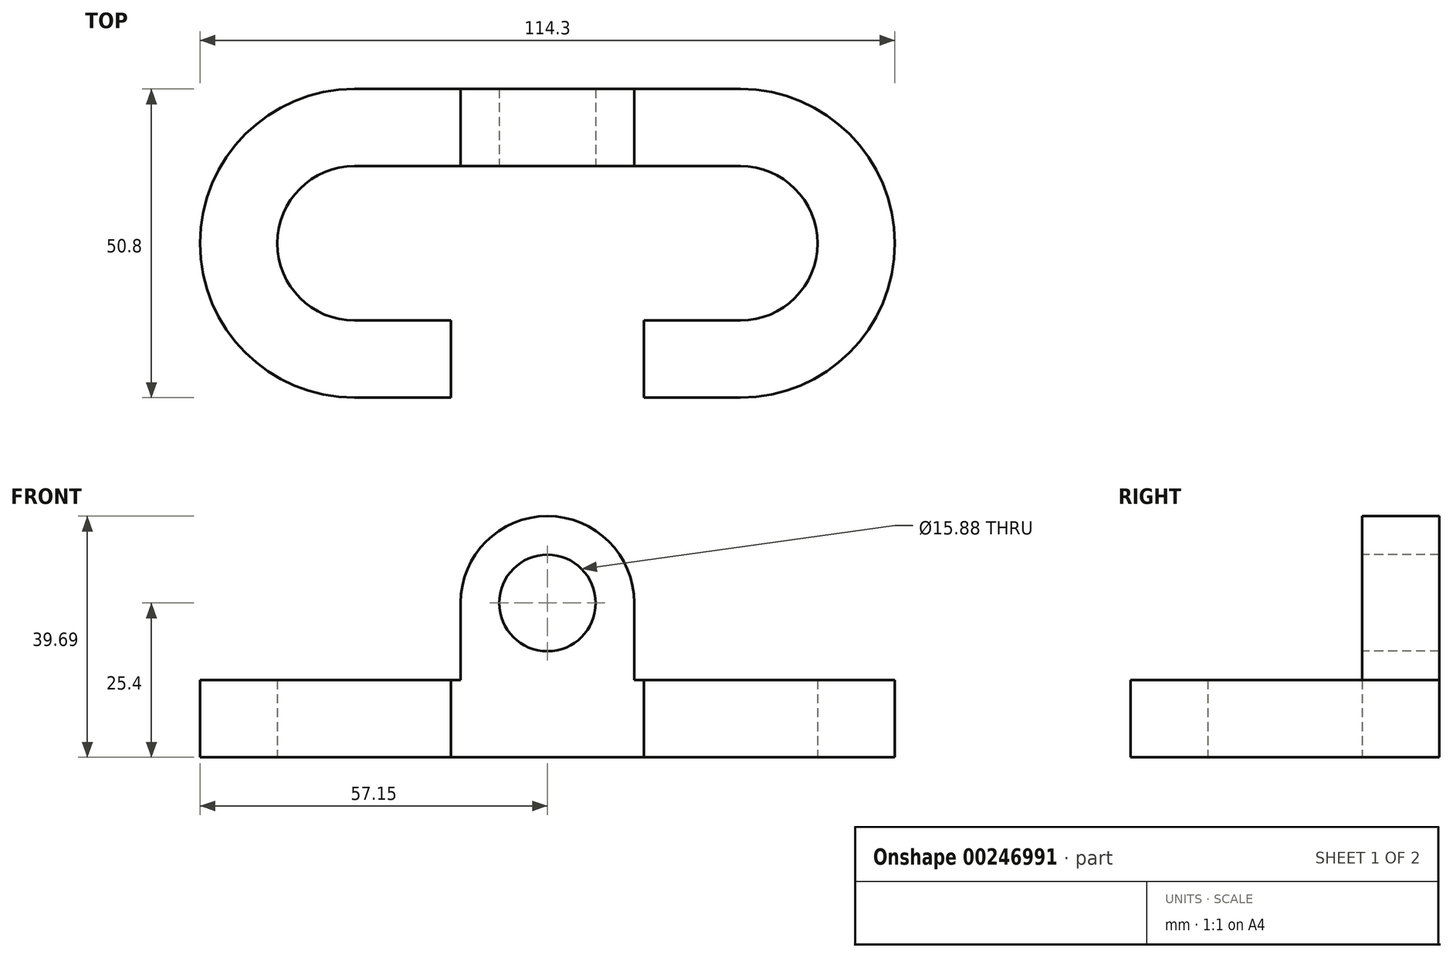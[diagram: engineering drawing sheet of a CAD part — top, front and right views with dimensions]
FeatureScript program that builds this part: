
annotation { "Feature Type Name" : "Feature", "Feature Type Description" : "" }
export const myFeature = defineFeature(function(context is Context, id is Id, definition is map)
    precondition{}
    {
        {
            var Q0;
            Q0=qCreatedBy(makeId("Top.planeOp"),FACE);
            var sketch = newSketch(context, id + "F0", { "sketchPlane" : qUnion([Q0])});
            skArc(sketch, "E0", {"start": v(31.75, -12.7) * mm, "mid": v(44.45, 0) * mm, "end": v(31.75, 12.7) * mm});
            skArc(sketch, "E1", {"start": v(31.75, -25.4) * mm, "mid": v(57.15, 0) * mm, "end": v(31.75, 25.4) * mm});
            skLineSegment(sketch, "E2", {"start": v(31.75, 25.4) * mm, "end": v(0, 25.4) * mm});
            skLineSegment(sketch, "E3", {"start": v(31.75, 12.7) * mm, "end": v(0, 12.7) * mm});
            skLineSegment(sketch, "E4", {"start": v(31.75, -12.7) * mm, "end": v(15.88, -12.7) * mm});
            skLineSegment(sketch, "E5", {"start": v(31.75, -25.4) * mm, "end": v(15.88, -25.4) * mm});
            skLineSegment(sketch, "E6", {"start": v(15.88, -12.7) * mm, "end": v(15.88, -25.4) * mm});
            skLineSegment(sketch, "E7.MirrorCS", {"start": v(-31.75, 25.4) * mm, "end": v(0, 25.4) * mm});
            skLineSegment(sketch, "E8.MirrorCS", {"start": v(-31.75, 12.7) * mm, "end": v(0, 12.7) * mm});
            skArc(sketch, "E9.MirrorCS", {"start": v(-31.75, -25.4) * mm, "mid": v(-57.15, 0) * mm, "end": v(-31.75, 25.4) * mm});
            skArc(sketch, "E10.MirrorCS", {"start": v(-31.75, -12.7) * mm, "mid": v(-44.45, 0) * mm, "end": v(-31.75, 12.7) * mm});
            skLineSegment(sketch, "E11.MirrorCS", {"start": v(-31.75, -25.4) * mm, "end": v(-15.88, -25.4) * mm});
            skLineSegment(sketch, "E12.MirrorCS", {"start": v(-31.75, -12.7) * mm, "end": v(-15.88, -12.7) * mm});
            skLineSegment(sketch, "E13.MirrorCS", {"start": v(-15.88, -12.7) * mm, "end": v(-15.88, -25.4) * mm});
            skSolve(sketch);
        }
        {
            var Q0;
            Q0=makeQuery(id+"F0.imprint","IMPRINT",FACE,{"disambiguationData":[TD([[makeQuery(id+"F0.imprint","IMPRINT",EDGE,{"derivedFrom":sQuery(id+"F0.wireOp",EDGE,"E0")}),-1.0]])]});
            extrude(context, id + "F1", {"entities" : qUnion([Q0]), "depth" : 12.7 * mm});
        }
        {
            var Q0;
            Q0=makeQuery(id+"F1.opExtrude","SWEPT_FACE",FACE,{"disambiguationData":[OSD([sQuery(id+"F0.wireOp",EDGE,"E3"),sQuery(id+"F0.wireOp",EDGE,"E8.MirrorCS")])]});
            var sketch = newSketch(context, id + "F2", { "sketchPlane" : qUnion([Q0])});
            skCircle(sketch, "E14", {"center": v(0, 25.4) * mm, "radius": 7.94 * mm});
            skArc(sketch, "E15", {"start": v(14.29, 25.4) * mm, "mid": v(0, 39.69) * mm, "end": v(-14.29, 25.4) * mm});
            skLineSegment(sketch, "E16", {"start": v(-14.29, 25.4) * mm, "end": v(-14.29, 12.7) * mm});
            skLineSegment(sketch, "E17", {"start": v(14.29, 25.4) * mm, "end": v(14.29, 12.7) * mm});
            skSolve(sketch);
        }
        {
            var Q0;
            Q0=makeQuery(id+"F2.imprint","IMPRINT",FACE,{"disambiguationData":[TD([[makeQuery(id+"F2.imprint","IMPRINT",EDGE,{"derivedFrom":sQuery(id+"F2.wireOp",EDGE,"E14")}),-1.0]])]});
            extrude(context, id + "F3", {"entities" : qUnion([Q0]), "operationType" : NewBodyOperationType.ADD, "oppositeDirection" : true, "depth" : 12.7 * mm});
        }
    });
